# Revit family: FLOWAIR Elis G1-E-200_RFA_2019
name_source: partatom
category: Electrical Fixtures
units: mm (PartAtom-declared; Revit-internal decimal feet)

## family parameters
Always vertical = No
Cut with Voids When Loaded = No
Maintain Annotation Orientation = No
Part Type = Normal
Room Calculation Point = No
Round Connector Dimension = Use Diameter
Shared = No
Work Plane-Based = No

## types (3) — shared parameters
Description = Vratová clona
IP = 54
Load classification = Other
Manufacturer = Hydronic Systems Prague s.r.o.
Material = FLOWAIR-Galvanized steel
Model = Elis G1-E-200
Power ratio = 1
Power supply = 400 V
Product data = 14227; délka 200cm, elektrická
Type Comments = vnitřní instalace mimo prostor s nebezpečím výbuchu, IP54; max dosah 7,5m na 3 rychlost
URL = www.hydronic.cz
Weight of unit = 67.00 kg

## per-type parameters (varying)
| type | Air flow | Apparent load | Max current consumption | Temperature increase |
| Elis G1-E-200, 1 rychlost | 5200.0 m³/h | 720 VA | 2 A | 12 °C |
| Elis G1-E-200, 2 rychlost | 6300.0 m³/h | 1440 VA | 4 A | 9 °C |
| Elis G1-E-200, 3 rychlost | 8200.0 m³/h | 1680 VA | 4 A | 7 °C |

## geometry (parser evidence)
native form markers: Sweep x3
no freeform markers — native parametric forms only
